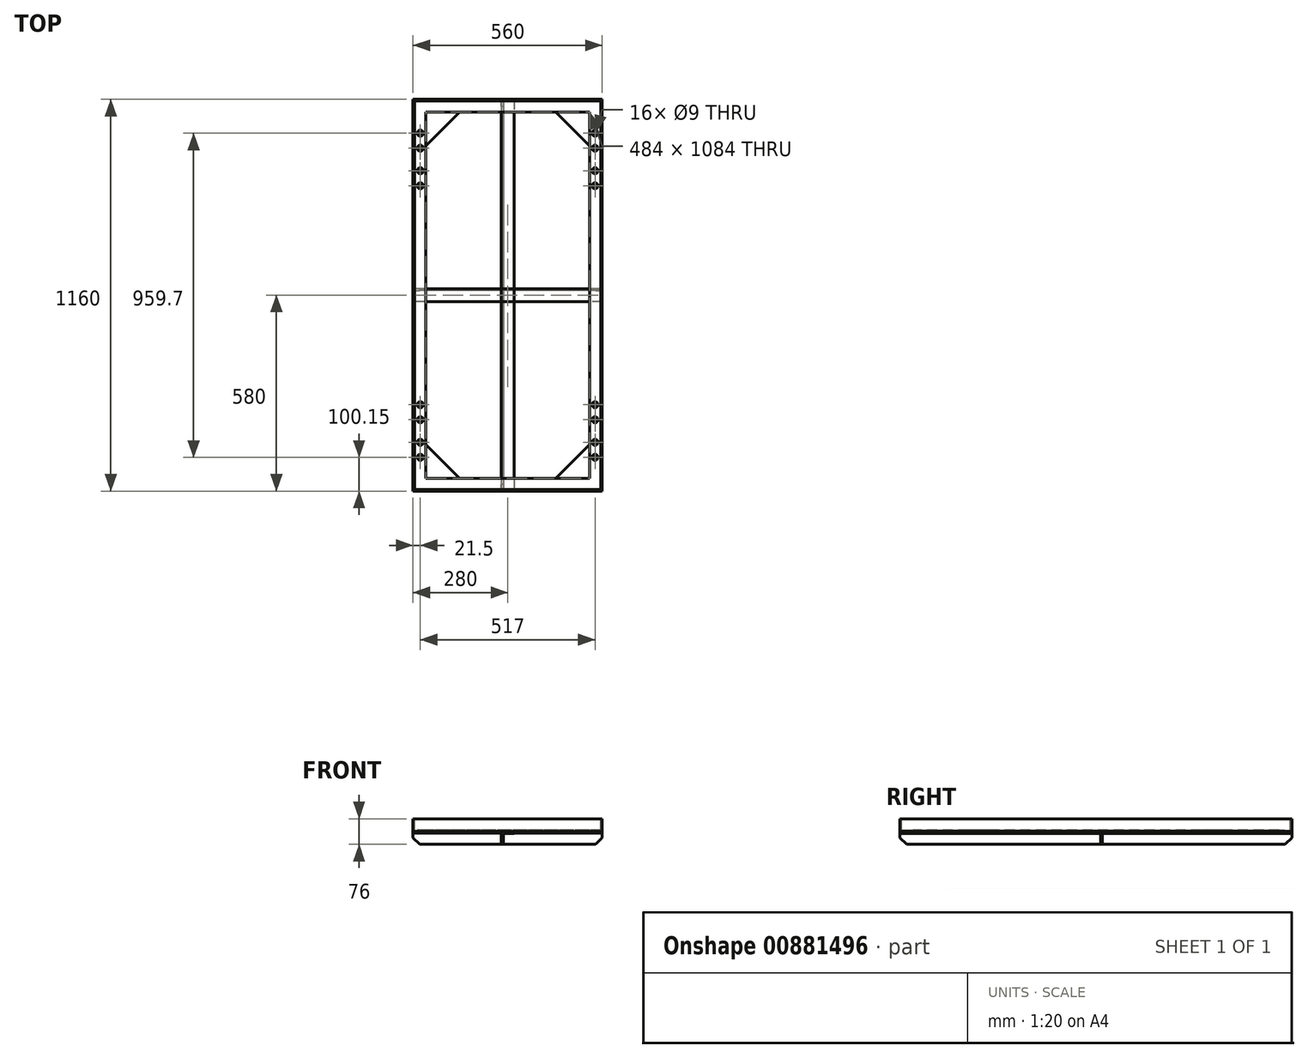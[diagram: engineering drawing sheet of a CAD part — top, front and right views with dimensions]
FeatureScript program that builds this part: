
annotation { "Feature Type Name" : "Feature", "Feature Type Description" : "" }
export const myFeature = defineFeature(function(context is Context, id is Id, definition is map)
    precondition{}
    {
        {
            var Q0;
            Q0=qCreatedBy(makeId("Top.planeOp"),FACE);
            var sketch = newSketch(context, id + "F0", { "sketchPlane" : qUnion([Q0])});
            skLineSegment(sketch, "E0.bottom", {"start": v(0, 0) * mm, "end": v(550, 0) * mm});
            skLineSegment(sketch, "E0.top", {"start": v(0, 1150) * mm, "end": v(550, 1150) * mm});
            skLineSegment(sketch, "E0.left", {"start": v(0, 0) * mm, "end": v(0, 1150) * mm});
            skLineSegment(sketch, "E0.right", {"start": v(550, 0) * mm, "end": v(550, 1150) * mm});
            skSolve(sketch);
        }
        {
            var Q0;
            Q0=qCreatedBy(makeId("Front.planeOp"),FACE);
            var sketch = newSketch(context, id + "F1", { "sketchPlane" : qUnion([Q0])});
            skLineSegment(sketch, "E1", {"start": v(0, 0) * mm, "end": v(0, 33) * mm});
            skLineSegment(sketch, "E2", {"start": v(0, 33) * mm, "end": v(-5, 33) * mm});
            skLineSegment(sketch, "E3", {"start": v(-5, 33) * mm, "end": v(-5, -5) * mm});
            skLineSegment(sketch, "E4", {"start": v(-5, -5) * mm, "end": v(33, -5) * mm});
            skLineSegment(sketch, "E5", {"start": v(33, -5) * mm, "end": v(33, 0) * mm});
            skLineSegment(sketch, "E6", {"start": v(33, 0) * mm, "end": v(0, 0) * mm});
            skSolve(sketch);
        }
        {
            var Q0;
            Q0 = qSketchRegion(id + "F1", true);
            var Q1;
            Q1 = qConstructionFilter(qBodyType(qCreatedBy(id + "F0" ,EDGE), BodyType.WIRE), ConstructionObject.NO);
            sweep(context, id + "F2", {"profiles" : qUnion([Q0]), "path" : qUnion([Q1])});
        }
        {
            var Q0;
            Q0=makeQuery(id+"F2.opSweep","SWEPT_FACE",FACE,{"disambiguationData":[OSD([sQuery(id+"F0.wireOp",EDGE,"E0.bottom"),sQuery(id+"F1.wireOp",EDGE,"E3")])]});
            var sketch = newSketch(context, id + "F3", { "sketchPlane" : qUnion([Q0])});
            skLineSegment(sketch, "E7", {"start": v(256, -5) * mm, "end": v(256, -43) * mm});
            skLineSegment(sketch, "E8", {"start": v(256, -43) * mm, "end": v(262, -43) * mm});
            skLineSegment(sketch, "E9", {"start": v(262, -43) * mm, "end": v(262, -11) * mm});
            skLineSegment(sketch, "E10", {"start": v(262, -11) * mm, "end": v(294, -11) * mm});
            skLineSegment(sketch, "E11", {"start": v(294, -11) * mm, "end": v(294, -5) * mm});
            skLineSegment(sketch, "E12", {"start": v(294, -5) * mm, "end": v(256, -5) * mm});
            skLineSegment(sketch, "E13", {"start": v(275, 33) * mm, "end": v(275, -5) * mm, "construction": true});
            skSolve(sketch);
        }
        {
            var Q0;
            Q0 = qSketchRegion(id + "F3", true);
            var Q1;
            Q1=makeQuery(id+"F2.opSweep","SWEPT_FACE",FACE,{"disambiguationData":[OSD([sQuery(id+"F0.wireOp",EDGE,"E0.top"),sQuery(id+"F1.wireOp",EDGE,"E3")])]});
            extrude(context, id + "F4", {"entities" : qUnion([Q0]), "endBound" : BoundingType.UP_TO_SURFACE, "oppositeDirection" : true, "depth" : 25 * mm, "endBoundEntityFace" : qUnion([Q1]), "offsetDistance" : 25 * mm});
        }
        {
            var Q0;
            Q0=makeQuery(id+"F2.opSweep","SWEPT_FACE",FACE,{"disambiguationData":[OSD([sQuery(id+"F0.wireOp",EDGE,"E0.left"),sQuery(id+"F1.wireOp",EDGE,"E3")])]});
            var sketch = newSketch(context, id + "F5", { "sketchPlane" : qUnion([Q0])});
            skLineSegment(sketch, "E14", {"start": v(-575, 33) * mm, "end": v(-575, -5) * mm, "construction": true});
            skLineSegment(sketch, "E15", {"start": v(-594, -43) * mm, "end": v(-594, -5) * mm});
            skLineSegment(sketch, "E16", {"start": v(-594, -5) * mm, "end": v(-556, -5) * mm});
            skLineSegment(sketch, "E17", {"start": v(-556, -5) * mm, "end": v(-556, -10) * mm});
            skLineSegment(sketch, "E18", {"start": v(-556, -10) * mm, "end": v(-589, -10) * mm});
            skLineSegment(sketch, "E19", {"start": v(-589, -10) * mm, "end": v(-589, -43) * mm});
            skLineSegment(sketch, "E20", {"start": v(-589, -43) * mm, "end": v(-594, -43) * mm});
            skSolve(sketch);
        }
        {
            var Q0;
            Q0 = qSketchRegion(id + "F5", true);
            var Q1;
            Q1=makeQuery(id+"F2.opSweep","SWEPT_FACE",FACE,{"disambiguationData":[OSD([sQuery(id+"F0.wireOp",EDGE,"E0.right"),sQuery(id+"F1.wireOp",EDGE,"E3")])]});
            extrude(context, id + "F6", {"entities" : qUnion([Q0]), "endBound" : BoundingType.UP_TO_SURFACE, "oppositeDirection" : true, "depth" : 25 * mm, "endBoundEntityFace" : qUnion([Q1]), "offsetDistance" : 25 * mm});
        }
        {
            var Q0;
            Q0=makeQuery(id+"F2.opSweep","SWEPT_FACE",FACE,{"disambiguationData":[OSD([sQuery(id+"F0.wireOp",EDGE,"E0.left"),sQuery(id+"F1.wireOp",EDGE,"E4")])]});
            var sketch = newSketch(context, id + "F7", { "sketchPlane" : qUnion([Q0])});
            skLineSegment(sketch, "E21", {"start": v(533.5, 5) * mm, "end": v(533.5, -1155) * mm, "construction": true});
            skLineSegment(sketch, "E22", {"start": v(-5, -16.5) * mm, "end": v(555, -16.5) * mm, "construction": true});
            skLineSegment(sketch, "E23.bottom", {"start": v(520.8, -65) * mm, "end": v(546.2, -65) * mm});
            skLineSegment(sketch, "E23.top", {"start": v(520.8, -280.9) * mm, "end": v(546.2, -280.9) * mm});
            skLineSegment(sketch, "E23.left", {"start": v(520.8, -65) * mm, "end": v(520.8, -280.9) * mm});
            skLineSegment(sketch, "E23.right", {"start": v(546.2, -65) * mm, "end": v(546.2, -280.9) * mm});
            skPoint(sketch, "E24", {"position": v(533.5, -95.15) * mm});
            skPoint(sketch, "E25", {"position": v(533.5, -139.65) * mm});
            skPoint(sketch, "E26", {"position": v(533.5, -206.25) * mm});
            skPoint(sketch, "E27", {"position": v(533.5, -250.75) * mm});
            skLineSegment(sketch, "E28", {"start": v(546.2, -172.95) * mm, "end": v(520.8, -172.95) * mm, "construction": true});
            skLineSegment(sketch, "E29", {"start": v(275, 5) * mm, "end": v(275, -1155) * mm, "construction": true});
            skLineSegment(sketch, "E30.MirrorCS", {"start": v(29.2, -65) * mm, "end": v(3.8, -65) * mm});
            skLineSegment(sketch, "E31.MirrorCS", {"start": v(3.8, -65) * mm, "end": v(3.8, -280.9) * mm});
            skLineSegment(sketch, "E32.MirrorCS", {"start": v(29.2, -65) * mm, "end": v(29.2, -280.9) * mm});
            skPoint(sketch, "E33.MirrorP", {"position": v(16.5, -95.15) * mm});
            skPoint(sketch, "E34.MirrorP", {"position": v(16.5, -139.65) * mm});
            skPoint(sketch, "E35.MirrorP", {"position": v(16.5, -206.25) * mm});
            skPoint(sketch, "E36.MirrorP", {"position": v(16.5, -250.75) * mm});
            skLineSegment(sketch, "E37.MirrorCS", {"start": v(29.2, -280.9) * mm, "end": v(3.8, -280.9) * mm});
            skLineSegment(sketch, "E38", {"start": v(-5, -575) * mm, "end": v(555, -575) * mm, "construction": true});
            skLineSegment(sketch, "E39.MirrorCS", {"start": v(29.2, -1085) * mm, "end": v(3.8, -1085) * mm});
            skLineSegment(sketch, "E40.MirrorCS", {"start": v(3.8, -1085) * mm, "end": v(3.8, -869.1) * mm});
            skLineSegment(sketch, "E41.MirrorCS", {"start": v(29.2, -1085) * mm, "end": v(29.2, -869.1) * mm});
            skPoint(sketch, "E42.MirrorP", {"position": v(16.5, -1054.85) * mm});
            skPoint(sketch, "E43.MirrorP", {"position": v(16.5, -1010.35) * mm});
            skPoint(sketch, "E44.MirrorP", {"position": v(16.5, -943.75) * mm});
            skPoint(sketch, "E45.MirrorP", {"position": v(16.5, -899.25) * mm});
            skLineSegment(sketch, "E46.MirrorCS", {"start": v(29.2, -869.1) * mm, "end": v(3.8, -869.1) * mm});
            skLineSegment(sketch, "E47.MirrorCS", {"start": v(520.8, -1085) * mm, "end": v(546.2, -1085) * mm});
            skLineSegment(sketch, "E48.MirrorCS", {"start": v(546.2, -1085) * mm, "end": v(546.2, -869.1) * mm});
            skLineSegment(sketch, "E49.MirrorCS", {"start": v(520.8, -1085) * mm, "end": v(520.8, -869.1) * mm});
            skPoint(sketch, "E50.MirrorP", {"position": v(533.5, -1054.85) * mm});
            skPoint(sketch, "E51.MirrorP", {"position": v(533.5, -1010.35) * mm});
            skPoint(sketch, "E52.MirrorP", {"position": v(533.5, -943.75) * mm});
            skPoint(sketch, "E53.MirrorP", {"position": v(533.5, -899.25) * mm});
            skLineSegment(sketch, "E54.MirrorCS", {"start": v(520.8, -869.1) * mm, "end": v(546.2, -869.1) * mm});
            skSolve(sketch);
        }
        {
            var Q0;
            Q0=makeQuery(id+"F2.opSweep","SWEPT_FACE",FACE,{"disambiguationData":[OSD([sQuery(id+"F0.wireOp",EDGE,"E0.left"),sQuery(id+"F1.wireOp",EDGE,"E6")])]});
            var sketch = newSketch(context, id + "F8", { "sketchPlane" : qUnion([Q0])});
            skPoint(sketch, "E55.0", {"position": v(533.5, 1054.85) * mm});
            skPoint(sketch, "E55.1", {"position": v(533.5, 1010.35) * mm});
            skPoint(sketch, "E55.2", {"position": v(533.5, 943.75) * mm});
            skPoint(sketch, "E55.3", {"position": v(533.5, 899.25) * mm});
            skPoint(sketch, "E55.4", {"position": v(533.5, 250.75) * mm});
            skPoint(sketch, "E55.5", {"position": v(533.5, 206.25) * mm});
            skPoint(sketch, "E55.6", {"position": v(533.5, 139.65) * mm});
            skPoint(sketch, "E55.7", {"position": v(533.5, 95.15) * mm});
            skPoint(sketch, "E55.8", {"position": v(16.5, 1054.85) * mm});
            skPoint(sketch, "E55.9", {"position": v(16.5, 1010.35) * mm});
            skPoint(sketch, "E55.10", {"position": v(16.5, 943.75) * mm});
            skPoint(sketch, "E55.11", {"position": v(16.5, 899.25) * mm});
            skPoint(sketch, "E55.12", {"position": v(16.5, 250.75) * mm});
            skPoint(sketch, "E55.13", {"position": v(16.5, 206.25) * mm});
            skPoint(sketch, "E55.14", {"position": v(16.5, 139.65) * mm});
            skPoint(sketch, "E55.15", {"position": v(16.5, 95.15) * mm});
            skSolve(sketch);
        }
        {
            var Q0;
            Q0=sQuery(id+"F8.wireOp",VERTEX,"E55.0");
            var Q1;
            Q1=sQuery(id+"F8.wireOp",VERTEX,"E55.1");
            var Q2;
            Q2=sQuery(id+"F8.wireOp",VERTEX,"E55.2");
            var Q3;
            Q3=sQuery(id+"F8.wireOp",VERTEX,"E55.3");
            var Q4;
            Q4=sQuery(id+"F8.wireOp",VERTEX,"E55.8");
            var Q5;
            Q5=sQuery(id+"F8.wireOp",VERTEX,"E55.9");
            var Q6;
            Q6=sQuery(id+"F8.wireOp",VERTEX,"E55.10");
            var Q7;
            Q7=sQuery(id+"F8.wireOp",VERTEX,"E55.11");
            var Q8;
            Q8=sQuery(id+"F8.wireOp",VERTEX,"E55.4");
            var Q9;
            Q9=sQuery(id+"F8.wireOp",VERTEX,"E55.5");
            var Q10;
            Q10=sQuery(id+"F8.wireOp",VERTEX,"E55.6");
            var Q11;
            Q11=sQuery(id+"F8.wireOp",VERTEX,"E55.7");
            var Q12;
            Q12=sQuery(id+"F8.wireOp",VERTEX,"E55.12");
            var Q13;
            Q13=sQuery(id+"F8.wireOp",VERTEX,"E55.13");
            var Q14;
            Q14=sQuery(id+"F8.wireOp",VERTEX,"E55.14");
            var Q15;
            Q15=sQuery(id+"F8.wireOp",VERTEX,"E55.15");
            var Q16;
            Q16=makeQuery(id+"F2.opSweep","SWEPT_BODY",BODY,{"disambiguationData":[OSD([sQuery(id+"F0.wireOp",EDGE,"E0.right"),sQuery(id+"F1.wireOp",EDGE,"E1"),sQuery(id+"F1.wireOp",EDGE,"E2"),sQuery(id+"F1.wireOp",EDGE,"E3"),sQuery(id+"F1.wireOp",EDGE,"E4"),sQuery(id+"F1.wireOp",EDGE,"E5"),sQuery(id+"F1.wireOp",EDGE,"E6")])]});
            hole(context, id + "F9", {"style" : HoleStyle.C_SINK, "endStyle" : HoleEndStyle.THROUGH, "standardTappedOrClearance" : lookupTablePath({ "fit" : "Normal", "standard" : "ISO", "size" : "M8", "type" : "Clearance" }), "standardBlindInLast" : lookupTablePath({ "fit" : "Normal", "standard" : "ISO", "size" : "M8", "type" : "Clearance" }), "holeDiameter" : 9 * mm, "cSinkDiameter" : 17.92 * mm, "cSinkAngle" : 90 * degree, "majorDiameter" : 5 * mm, "isTappedThrough" : true, "tappedDepth" : 12 * mm, "tapClearance" : 3, "locations" : qUnion([Q0, Q1, Q2, Q3, Q4, Q5, Q6, Q7, Q8, Q9, Q10, Q11, Q12, Q13, Q14, Q15]), "scope" : qUnion([Q16])});
        }
        {
            var Q0;
            Q0=makeQuery(id+"F2.opSweep","SWEPT_FACE",FACE,{"disambiguationData":[OSD([sQuery(id+"F0.wireOp",EDGE,"E0.left"),sQuery(id+"F1.wireOp",EDGE,"E4")])]});
            var sketch = newSketch(context, id + "F10", { "sketchPlane" : qUnion([Q0])});
            skSolve(sketch);
        }
        {
            var Q0;
            {var subQ0=sQuery(id+"F1.wireOp",EDGE,"E4");var subQ18=sQuery(id+"F1.wireOp",EDGE,"E3");var subQ19=sQuery(id+"F0.wireOp",EDGE,"E0.bottom");Q0=makeQuery(id+"F10.imprint","IMPRINT",FACE,{"disambiguationData":[TD([[makeQuery(id+"F10.imprint","IMPRINT",EDGE,{"derivedFrom":makeQuery(id+"F2.opSweep","SWEPT_EDGE",EDGE,{"disambiguationData":[OSD([subQ19,subQ18,subQ0])]})}),1.0]])]});}
            var sketch = newSketch(context, id + "F11", { "sketchPlane" : qUnion([Q0])});
            skLineSegment(sketch, "E56", {"start": v(517, -1017) * mm, "end": v(417, -1117) * mm});
            skLineSegment(sketch, "E57", {"start": v(417, -1117) * mm, "end": v(517, -1117) * mm});
            skLineSegment(sketch, "E58", {"start": v(517, -1117) * mm, "end": v(517, -1017) * mm});
            skLineSegment(sketch, "E59", {"start": v(133, -1117) * mm, "end": v(33, -1017) * mm});
            skLineSegment(sketch, "E60", {"start": v(33, -1017) * mm, "end": v(33, -1117) * mm});
            skLineSegment(sketch, "E61", {"start": v(133, -1117) * mm, "end": v(33, -1117) * mm});
            skLineSegment(sketch, "E62", {"start": v(517, -133) * mm, "end": v(517, -33) * mm});
            skLineSegment(sketch, "E63", {"start": v(517, -33) * mm, "end": v(417, -33) * mm});
            skLineSegment(sketch, "E64", {"start": v(417, -33) * mm, "end": v(517, -133) * mm});
            skLineSegment(sketch, "E65", {"start": v(133, -33) * mm, "end": v(33, -33) * mm});
            skLineSegment(sketch, "E66", {"start": v(33, -33) * mm, "end": v(33, -133) * mm});
            skLineSegment(sketch, "E67", {"start": v(33, -133) * mm, "end": v(133, -33) * mm});
            skSolve(sketch);
        }
        {
            var Q0;
            Q0=makeQuery(id+"F6.opExtrude","CAP_EDGE",EDGE,{"disambiguationData":[OSD([sQuery(id+"F5.wireOp",EDGE,"E20")])],"isStart":false});
            var Q1;
            Q1=makeQuery(id+"F4.opExtrude","CAP_EDGE",EDGE,{"disambiguationData":[OSD([sQuery(id+"F3.wireOp",EDGE,"E8")])],"isStart":false});
            var Q2;
            Q2=makeQuery(id+"F6.opExtrude","CAP_EDGE",EDGE,{"disambiguationData":[OSD([sQuery(id+"F5.wireOp",EDGE,"E20")])],"isStart":true});
            var Q3;
            Q3=makeQuery(id+"F4.opExtrude","CAP_EDGE",EDGE,{"disambiguationData":[OSD([sQuery(id+"F3.wireOp",EDGE,"E8")])],"isStart":true});
            chamfer(context, id + "F12", {"entities" : qUnion([Q0, Q1, Q2, Q3]), "width" : 20 * mm, "tangentPropagation" : true});
        }
        {
            var Q0;
            Q0 = qSketchRegion(id + "F11", true);
            var Q1;
            Q1=makeQuery(id+"F2.opSweep","SWEPT_FACE",FACE,{"disambiguationData":[OSD([sQuery(id+"F0.wireOp",EDGE,"E0.left"),sQuery(id+"F1.wireOp",EDGE,"E6")])]});
            extrude(context, id + "F13", {"entities" : qUnion([Q0]), "endBound" : BoundingType.UP_TO_SURFACE, "oppositeDirection" : true, "depth" : 25 * mm, "endBoundEntityFace" : qUnion([Q1]), "offsetDistance" : 25 * mm});
        }
    });
